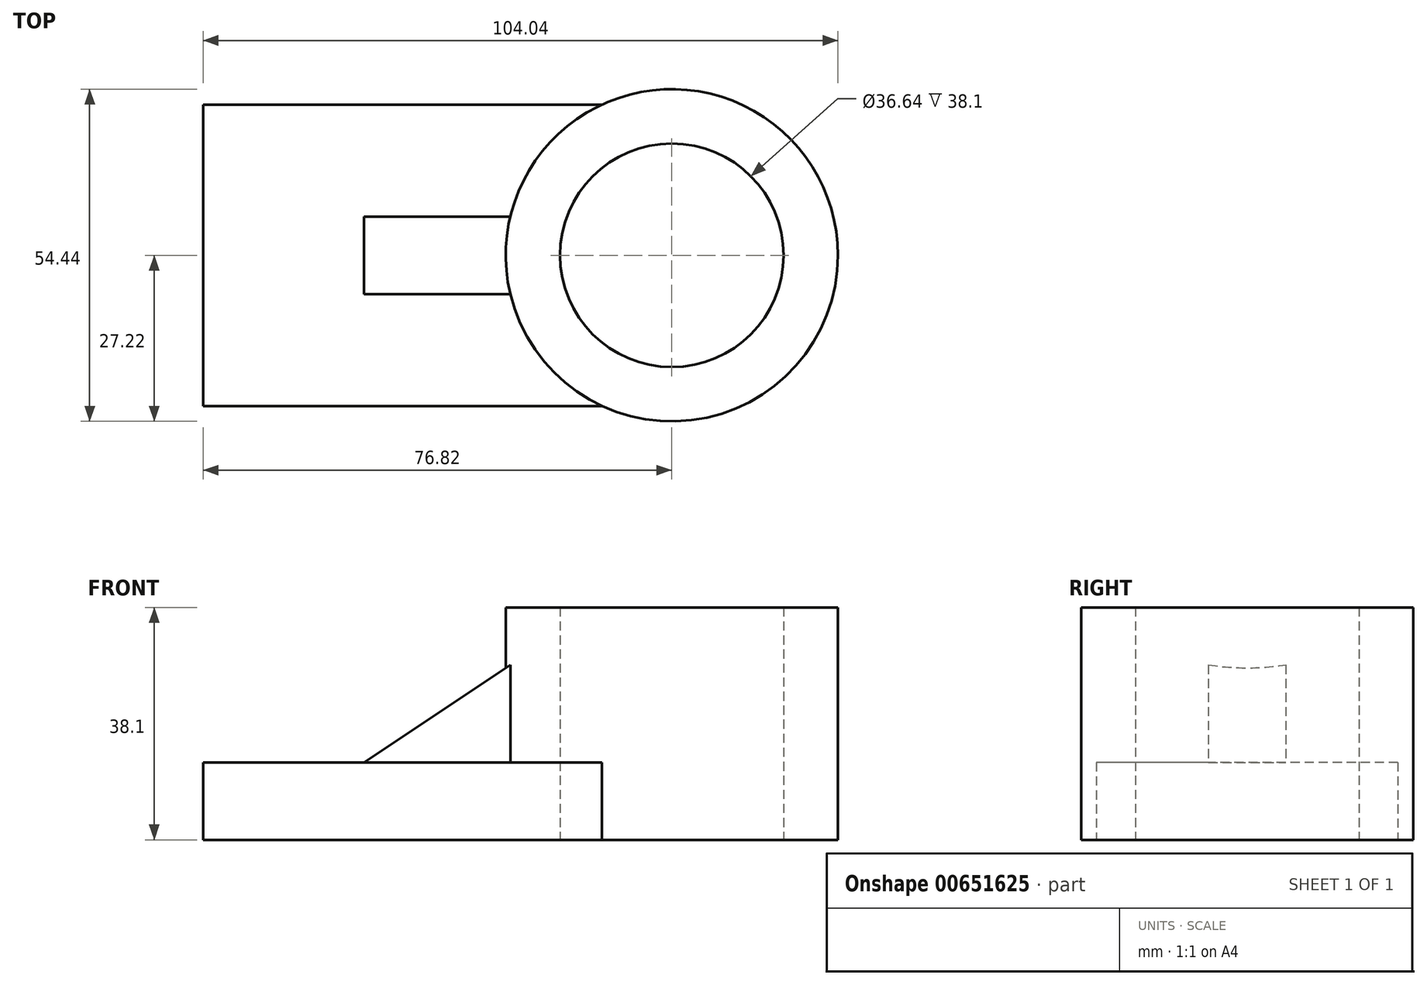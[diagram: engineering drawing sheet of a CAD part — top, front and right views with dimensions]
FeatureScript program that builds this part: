
annotation { "Feature Type Name" : "Feature", "Feature Type Description" : "" }
export const myFeature = defineFeature(function(context is Context, id is Id, definition is map)
    precondition{}
    {
        {
            var Q0;
            Q0=qCreatedBy(makeId("Top.planeOp"),FACE);
            var sketch = newSketch(context, id + "F0", { "sketchPlane" : qUnion([Q0])});
            skLineSegment(sketch, "E0.bottom", {"start": v(26.98, 24.7) * mm, "end": v(-38.4, 24.7) * mm});
            skLineSegment(sketch, "E0.top", {"start": v(26.98, -24.7) * mm, "end": v(-38.4, -24.7) * mm});
            skLineSegment(sketch, "E0.right", {"start": v(-38.4, 24.7) * mm, "end": v(-38.4, -24.7) * mm});
            skPoint(sketch, "E0.middle", {"position": v(0, 0) * mm});
            skCircle(sketch, "E1", {"center": v(38.4, 0) * mm, "radius": 27.22 * mm});
            skCircle(sketch, "E2", {"center": v(38.4, 0) * mm, "radius": 18.32 * mm});
            skPoint(sketch, "E3.orphan", {"position": v(38.4, 24.7) * mm});
            skPoint(sketch, "E4.orphan", {"position": v(38.4, -24.7) * mm});
            skSolve(sketch);
        }
        {
            var Q0;
            Q0=makeQuery(id+"F0.imprint","IMPRINT",FACE,{"disambiguationData":[TD([[makeQuery(id+"F0.imprint","IMPRINT",EDGE,{"derivedFrom":sQuery(id+"F0.wireOp",EDGE,"E2")}),-1.0]])]});
            extrude(context, id + "F1", {"entities" : qUnion([Q0]), "depth" : 38.1 * mm, "offsetDistance" : 25.4 * mm});
        }
        {
            var Q0;
            {var subQ0=sQuery(id+"F0.wireOp",EDGE,"E0.bottom");Q0=makeQuery(id+"F0.imprint","IMPRINT",FACE,{"disambiguationData":[TD([[makeQuery(id+"F0.imprint","IMPRINT",EDGE,{"derivedFrom":subQ0}),1.0]])]});}
            extrude(context, id + "F2", {"entities" : qUnion([Q0]), "operationType" : NewBodyOperationType.ADD, "depth" : 12.7 * mm, "offsetDistance" : 25.4 * mm});
        }
        {
            var Q0;
            Q0=qCreatedBy(makeId("Front.planeOp"),FACE);
            var sketch = newSketch(context, id + "F3", { "sketchPlane" : qUnion([Q0])});
            skLineSegment(sketch, "E5", {"start": v(14.3, 30.26) * mm, "end": v(-17.31, 9.18) * mm});
            skLineSegment(sketch, "E6", {"start": v(-17.31, 9.18) * mm, "end": v(14.3, 9.18) * mm});
            skLineSegment(sketch, "E7", {"start": v(14.3, 9.18) * mm, "end": v(14.3, 30.26) * mm});
            skSolve(sketch);
        }
        {
            var Q0;
            Q0 = qSketchRegion(id + "F3", true);
            extrude(context, id + "F4", {"entities" : qUnion([Q0]), "operationType" : NewBodyOperationType.ADD, "endBound" : BoundingType.SYMMETRIC, "depth" : 12.7 * mm, "offsetDistance" : 25.4 * mm});
        }
    });
